# Revit family: Mailboxes_4C-Salsbury_Industries-Pedestal_Mounted-12_Door_High_Units
name_source: partatom
category: Specialty Equipment
revit_build: Autodesk Revit 2016 (Build: 20150714_1515(x64)
units: mm (PartAtom-declared; Revit-internal decimal feet)

## family parameters
Always vertical = Yes
Cut with Voids When Loaded = No
OmniClass Number = 23.40.90.14.11
OmniClass Title = Mail Boxes
Part Type = Normal
Room Calculation Point = No
Round Connector Dimension = Use Diameter
Shared = No
Work Plane-Based = No

## types (9) — shared parameters
4C Unit Elevation = 13.5 "
4C Unit Height = 44.5 "
Assembly Code = C1030910
Assembly Description = Mailboxes
Depth = 19 "
Height = 59.75 "
Lock Material = Stainless Steel - Salsbury Finish -  Polished
Manufacturer = Salsbury Industries
MasterFormat Number = 10 55 00
MasterFormat Title = Postal Specialties
OmniClass 23 Number = 23.40.90.14.11
OmniClass 23 Title = Mail Boxes
Type Comments = Pedestal Mounted 4C Horizontal Mailboxes - Front Loading
URL = www.mailboxes.com
Version = 1.0 (06/30/17)

## per-type parameters (varying)
| type | 4C Unit | Description | Pedestal Height | Width |
| 3412S-10 | Mailboxes_4C-Salsbury_Industries-Front_Load-12_Door_High_Units : 3712S-10 FL | 12 Door High Unit:  10 MB1, OM2 | 13 " | 17.496 " |
| 3412D-22 | Mailboxes_4C-Salsbury_Industries-Front_Load-12_Door_High_Units : 3712D-22 FL | 12 Door High Unit:  22 MB1, OM2 | 12.535 " | 32.25 " |
| 3412D-12 | Mailboxes_4C-Salsbury_Industries-Front_Load-12_Door_High_Units : 3712D-12 FL | 12 Door High Unit:  12 MB1, 2 PL5, OM2 | 12.535 " | 32.25 " |
| 3412D-11 | Mailboxes_4C-Salsbury_Industries-Front_Load-12_Door_High_Units : 3712D-11 FL | 12 Door High Unit:  11 MB1, 1 PL5, 1 PL6, OM2 | 12.535 " | 32.25 " |
| 3412D-10 | Mailboxes_4C-Salsbury_Industries-Front_Load-12_Door_High_Units : 3712D-10 FL | 12 Door High Unit:  10 MB1, 2 PL6, OM2 | 12.535 " | 32.25 " |
| 3412D-05 | Mailboxes_4C-Salsbury_Industries-Front_Load-12_Door_High_Units : 3712D-05 FL | 12 Door High Unit:  5 MB2, 2 PL6, OM2 | 12.535 " | 32.25 " |
| 3412D-4P | Mailboxes_4C-Salsbury_Industries-Front_Load-12_Door_High_Units : 3712D-4P FL | 12 Door High Unit:  4 PL6 | 12.535 " | 32.25 " |
| 3412S-02 | Mailboxes_4C-Salsbury_Industries-Front_Load-12_Door_High_Units : 3712S-02 FL | 12 Door High Unit:  2 MB2, 1 PL6, OM2 | 12.535 " | 17.496 " |
| 3412S-2P | Mailboxes_4C-Salsbury_Industries-Front_Load-12_Door_High_Units : 3712S-2P FL | 12 Door High Unit:  2 PL6 | 12.535 " | 17.496 " |

note: column(s) folded — value = type name in every type: Model

## geometry (parser evidence)
native form markers: Blend x6, Extrusion x4, Sweep x12
no freeform markers — native parametric forms only
